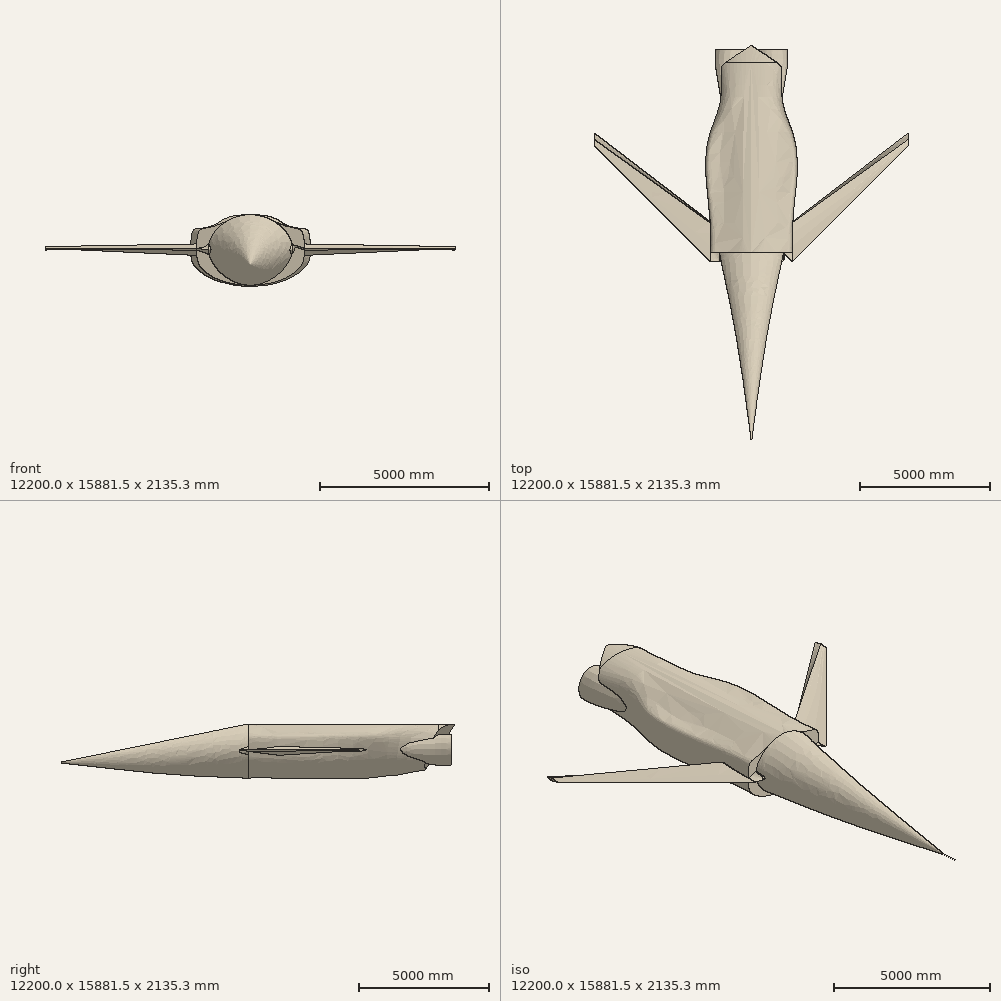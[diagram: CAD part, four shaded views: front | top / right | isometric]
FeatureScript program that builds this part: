
annotation { "Feature Type Name" : "Feature", "Feature Type Description" : "" }
export const myFeature = defineFeature(function(context is Context, id is Id, definition is map)
    precondition{}
    {
        {
            var Q0;
            Q0=qCreatedBy(makeId("Right.planeOp"),FACE);
            var sketch = newSketch(context, id + "F0", { "sketchPlane" : qUnion([Q0])});
            skLineSegment(sketch, "E0", {"start": v(0, 0) * mm, "end": v(-1750, 0) * mm});
            skLineSegment(sketch, "E1", {"start": v(-1750, 0) * mm, "end": v(-3500, 0) * mm});
            skLineSegment(sketch, "E2", {"start": v(-3500, 0) * mm, "end": v(-3500, -1000) * mm});
            skLineSegment(sketch, "E3", {"start": v(-3500, -1000) * mm, "end": v(-8500, -1000) * mm});
            skLineSegment(sketch, "E4", {"start": v(-8500, -1000) * mm, "end": v(-8500, -499.31) * mm});
            skLineSegment(sketch, "E5", {"start": v(-1151.4, 0) * mm, "end": v(-1151.4, 1000) * mm});
            skLineSegment(sketch, "E6", {"start": v(-1151.4, 1000) * mm, "end": v(-8500, -499.31) * mm});
            skLineSegment(sketch, "E7", {"start": v(-8500, -499.31) * mm, "end": v(-3500, -1000) * mm});
            skLineSegment(sketch, "E8", {"start": v(-3500, 0) * mm, "end": v(-3500, 520.82) * mm});
            skLineSegment(sketch, "E9", {"start": v(-8500, -499.31) * mm, "end": v(-8450, -499.31) * mm});
            skLineSegment(sketch, "E10", {"start": v(-8450, -499.31) * mm, "end": v(-8450, -489.1) * mm});
            skLineSegment(sketch, "E11", {"start": v(-8450, -499.31) * mm, "end": v(-8450, -504.32) * mm});
            skSolve(sketch);
        }
        {
            var Q0;
            Q0=sQuery(id+"F0.wireOp",EDGE,"E5");
            cPlane(context, id + "F1", {"entities" : qUnion([Q0]), "cplaneType" : CPlaneType.LINE_ANGLE, "offset" : 25 * mm, "angle" : 90 * degree, "oppositeDirection" : true, "width" : 150 * mm, "height" : 150 * mm});
        }
        {
            var Q0;
            Q0=qCreatedBy(id+"F1.planeOp",FACE);
            var sketch = newSketch(context, id + "F2", { "sketchPlane" : qUnion([Q0])});
            skPoint(sketch, "E12.middle", {"position": v(0, 0) * mm});
            skFitSpline(sketch, "E13", {"points": [v(0, 1000) * mm, v(-1060, 662.5) * mm, v(-1517.6, 506.84) * mm, v(-1600, 0) * mm, v(-1517.6, -506.84) * mm, v(-750, -1000) * mm, v(750, -1000) * mm, v(1517.6, -506.84) * mm, v(1600, 0) * mm, v(1517.6, 506.84) * mm, v(1060, 662.5) * mm, v(0, 1000) * mm]});
            skSolve(sketch);
        }
        {
            var Q0;
            Q0=qCreatedBy(makeId("Front.planeOp"),FACE);
            var sketch = newSketch(context, id + "F3", { "sketchPlane" : qUnion([Q0])});
            skPoint(sketch, "E14.middle", {"position": v(0, 0) * mm});
            skFitSpline(sketch, "E15", {"points": [v(0, 1000) * mm, v(-1060, 662.5) * mm, v(-1517.6, 506.84) * mm, v(-1600, 0) * mm, v(-1517.6, -506.84) * mm, v(-750, -1000) * mm, v(750, -1000) * mm, v(1517.6, -506.84) * mm, v(1600, 0) * mm, v(1517.6, 506.84) * mm, v(1060, 662.5) * mm, v(0, 1000) * mm]});
            skSolve(sketch);
        }
        {
            var Q0;
            Q0=qCreatedBy(makeId("Front.planeOp"),FACE);
            cPlane(context, id + "F4", {"entities" : qUnion([Q0]), "cplaneType" : CPlaneType.OFFSET, "offset" : 3500 * mm, "oppositeDirection" : true, "width" : 150 * mm, "height" : 150 * mm});
        }
        {
            var Q0;
            Q0=qCreatedBy(id+"F4.planeOp",FACE);
            var sketch = newSketch(context, id + "F5", { "sketchPlane" : qUnion([Q0])});
            skPoint(sketch, "E16.middle", {"position": v(0, 0) * mm});
            skFitSpline(sketch, "E17", {"points": [v(0, 1000) * mm, v(-1060, 662.5) * mm, v(-1517.6, 506.84) * mm, v(-1600, 0) * mm, v(-1517.6, -506.84) * mm, v(-750, -1000) * mm, v(750, -1000) * mm, v(1517.6, -506.84) * mm, v(1600, 0) * mm, v(1517.6, 506.84) * mm, v(1060, 662.5) * mm, v(0, 1000) * mm]});
            skSolve(sketch);
        }
        {
            var Q0;
            Q0=qCreatedBy(makeId("Front.planeOp"),FACE);
            cPlane(context, id + "F6", {"entities" : qUnion([Q0]), "cplaneType" : CPlaneType.OFFSET, "offset" : 4500 * mm, "oppositeDirection" : true, "width" : 150 * mm, "height" : 150 * mm});
        }
        {
            var Q0;
            Q0=qCreatedBy(id+"F6.planeOp",FACE);
            var sketch = newSketch(context, id + "F7", { "sketchPlane" : qUnion([Q0])});
            skPoint(sketch, "E18.middle", {"position": v(0, 0) * mm});
            skFitSpline(sketch, "E19", {"points": [v(0, 1000) * mm, v(-1060, 662.5) * mm, v(-1250, 0) * mm, v(-1060, -662.5) * mm, v(0, -1000) * mm, v(1060, -662.5) * mm, v(1250, 0) * mm, v(1060, 662.5) * mm, v(0, 1000) * mm]});
            skSolve(sketch);
        }
        {
            var Q0;
            Q0=qCreatedBy(makeId("Front.planeOp"),FACE);
            cPlane(context, id + "F8", {"entities" : qUnion([Q0]), "cplaneType" : CPlaneType.OFFSET, "offset" : 6232.05 * mm, "oppositeDirection" : true, "width" : 150 * mm, "height" : 150 * mm});
        }
        {
            var Q0;
            Q0=qCreatedBy(id+"F8.planeOp",FACE);
            var sketch = newSketch(context, id + "F9", { "sketchPlane" : qUnion([Q0])});
            skPoint(sketch, "E20.middle", {"position": v(0, 0) * mm});
            skFitSpline(sketch, "E21", {"points": [v(0, 1000) * mm, v(-1060, 662.5) * mm, v(-1250, 0) * mm, v(-848, -530) * mm, v(848, -530) * mm, v(1250, 0) * mm, v(1060, 662.5) * mm, v(0, 1000) * mm]});
            skSolve(sketch);
        }
        {
            var Q0;
            Q0=makeQuery(id+"F2.imprint","IMPRINT",FACE,{"disambiguationData":[TD([[makeQuery(id+"F2.imprint","IMPRINT",EDGE,{"derivedFrom":sQuery(id+"F2.wireOp",EDGE,"E13")}),1.0]])]});
            var Q1;
            Q1=makeQuery(id+"F3.imprint","IMPRINT",FACE,{"disambiguationData":[TD([[makeQuery(id+"F3.imprint","IMPRINT",EDGE,{"derivedFrom":sQuery(id+"F3.wireOp",EDGE,"E15")}),1.0]])]});
            var Q2;
            Q2=makeQuery(id+"F5.imprint","IMPRINT",FACE,{"disambiguationData":[TD([[makeQuery(id+"F5.imprint","IMPRINT",EDGE,{"derivedFrom":sQuery(id+"F5.wireOp",EDGE,"E17")}),1.0]])]});
            var Q3;
            Q3=makeQuery(id+"F7.imprint","IMPRINT",FACE,{"disambiguationData":[TD([[makeQuery(id+"F7.imprint","IMPRINT",EDGE,{"derivedFrom":sQuery(id+"F7.wireOp",EDGE,"E19")}),1.0]])]});
            var Q4;
            Q4=makeQuery(id+"F9.imprint","IMPRINT",FACE,{"disambiguationData":[TD([[makeQuery(id+"F9.imprint","IMPRINT",EDGE,{"derivedFrom":sQuery(id+"F9.wireOp",EDGE,"E21")}),1.0]])]});
            loft(context, id + "F10", {"sheetProfilesArray" : [{ "sheetProfileEntities" : qUnion([Q0]) }, { "sheetProfileEntities" : qUnion([Q1]) }, { "sheetProfileEntities" : qUnion([Q2]) }, { "sheetProfileEntities" : qUnion([Q3]) }, { "sheetProfileEntities" : qUnion([Q4]) }]});
        }
        {
            var Q0;
            Q0=makeQuery(id+"F10.opLoft","CAP_FACE",FACE,{"disambiguationData":[OSD([makeQuery(id+"F9.imprint","IMPRINT",FACE,{"disambiguationData":[TD([[makeQuery(id+"F9.imprint","IMPRINT",EDGE,{"derivedFrom":sQuery(id+"F9.wireOp",EDGE,"E21")}),1.0]])]})])],"isStart":true});
            extrude(context, id + "F11", {"entities" : qUnion([Q0]), "operationType" : NewBodyOperationType.ADD, "depth" : 649.4 * mm, "offsetDistance" : 25 * mm});
        }
        {
            var Q0;
            Q0=qCreatedBy(makeId("Right.planeOp"),FACE);
            var sketch = newSketch(context, id + "F12", { "sketchPlane" : qUnion([Q0])});
            skLineSegment(sketch, "E22", {"start": v(0, 0) * mm, "end": v(4500, 0) * mm});
            skLineSegment(sketch, "E23", {"start": v(4500, 0) * mm, "end": v(6232.05, 0) * mm});
            skLineSegment(sketch, "E24", {"start": v(4500, 0) * mm, "end": v(4500, 1000) * mm});
            skLineSegment(sketch, "E25", {"start": v(4500, 1000) * mm, "end": v(6881.46, 1000) * mm});
            skLineSegment(sketch, "E26", {"start": v(6881.46, 1000) * mm, "end": v(6881.46, -1000) * mm});
            skLineSegment(sketch, "E27", {"start": v(6881.46, 1000) * mm, "end": v(6232.05, 0) * mm});
            skLineSegment(sketch, "E28", {"start": v(6232.05, 0) * mm, "end": v(5582.64, -1000) * mm});
            skLineSegment(sketch, "E29", {"start": v(5582.64, -1000) * mm, "end": v(6881.46, -1000) * mm});
            skSolve(sketch);
        }
        {
            var Q0;
            Q0=makeQuery(id+"F12.imprint","IMPRINT",FACE,{"disambiguationData":[TD([[makeQuery(id+"F12.imprint","IMPRINT",EDGE,{"derivedFrom":sQuery(id+"F12.wireOp",EDGE,"E26")}),-1.0]])]});
            var Q1;
            Q1=sQuery(id+"F12.wireOp",EDGE,"E25");
            revolve(context, id + "F13", {"operationType" : NewBodyOperationType.REMOVE, "entities" : qUnion([Q0]), "axis" : qUnion([Q1]), "revolveType" : RevolveType.SYMMETRIC, "oppositeDirection" : true, "angle" : 182 * degree});
        }
        {
            var Q0;
            Q0=qCreatedBy(id+"F1.planeOp",FACE);
            var sketch = newSketch(context, id + "F14", { "sketchPlane" : qUnion([Q0])});
            skFitSpline(sketch, "E30", {"points": [v(0, 1000) * mm, v(-1250, 0) * mm, v(0, -1099.92) * mm, v(1250, 0) * mm, v(0, 1000) * mm]});
            skSolve(sketch);
        }
        {
            var Q0;
            Q0=qCreatedBy(makeId("Front.planeOp"),FACE);
            cPlane(context, id + "F15", {"entities" : qUnion([Q0]), "cplaneType" : CPlaneType.OFFSET, "offset" : 3500 * mm, "width" : 150 * mm, "height" : 150 * mm});
        }
        {
            var Q0;
            Q0=qCreatedBy(id+"F15.planeOp",FACE);
            var sketch = newSketch(context, id + "F16", { "sketchPlane" : qUnion([Q0])});
            skCircle(sketch, "E31", {"center": v(0, -239.59) * mm, "radius": 760.41 * mm});
            skSolve(sketch);
        }
        {
            var Q0;
            Q0=qCreatedBy(makeId("Front.planeOp"),FACE);
            cPlane(context, id + "F17", {"entities" : qUnion([Q0]), "cplaneType" : CPlaneType.OFFSET, "offset" : 8450 * mm, "width" : 150 * mm, "height" : 150 * mm});
        }
        {
            var Q0;
            Q0=qCreatedBy(id+"F17.planeOp",FACE);
            var sketch = newSketch(context, id + "F18", { "sketchPlane" : qUnion([Q0])});
            skCircle(sketch, "E32", {"center": v(0, -496.71) * mm, "radius": 7.6 * mm});
            skSolve(sketch);
        }
        {
            var Q1;
            Q1=makeQuery(id+"F18.imprint","IMPRINT",FACE,{"disambiguationData":[TD([[makeQuery(id+"F18.imprint","IMPRINT",EDGE,{"derivedFrom":sQuery(id+"F18.wireOp",EDGE,"E32")}),1.0]])]});
            var Q2;
            Q2=makeQuery(id+"F16.imprint","IMPRINT",FACE,{"disambiguationData":[TD([[makeQuery(id+"F16.imprint","IMPRINT",EDGE,{"derivedFrom":sQuery(id+"F16.wireOp",EDGE,"E31")}),1.0]])]});
            var Q3;
            Q3=makeQuery(id+"F14.imprint","IMPRINT",FACE,{"disambiguationData":[TD([[makeQuery(id+"F14.imprint","IMPRINT",EDGE,{"derivedFrom":sQuery(id+"F14.wireOp",EDGE,"E30")}),1.0]])]});
            loft(context, id + "F19", {"operationType" : NewBodyOperationType.ADD, "sheetProfilesArray" : [{ "sheetProfileEntities" : qUnion([Q1]) }, { "sheetProfileEntities" : qUnion([Q2]) }, { "sheetProfileEntities" : qUnion([Q3]) }]});
        }
        {
            var Q0;
            Q0=makeQuery(id+"F19.opLoft","CAP_FACE",FACE,{"disambiguationData":[OSD([makeQuery(id+"F18.imprint","IMPRINT",FACE,{"disambiguationData":[TD([[makeQuery(id+"F18.imprint","IMPRINT",EDGE,{"derivedFrom":sQuery(id+"F18.wireOp",EDGE,"E32")}),1.0]])]})])],"isStart":true});
            extrude(context, id + "F20", {"entities" : qUnion([Q0]), "operationType" : NewBodyOperationType.ADD, "depth" : 550 * mm, "offsetDistance" : 25 * mm});
        }
        {
            var Q0;
            Q0=qCreatedBy(makeId("Front.planeOp"),FACE);
            cPlane(context, id + "F21", {"entities" : qUnion([Q0]), "cplaneType" : CPlaneType.OFFSET, "offset" : 3500 * mm, "oppositeDirection" : true, "width" : 150 * mm, "height" : 150 * mm});
        }
        {
            var Q0;
            Q0=qCreatedBy(id+"F21.planeOp",FACE);
            var sketch = newSketch(context, id + "F22", { "sketchPlane" : qUnion([Q0])});
            skCircle(sketch, "E33", {"center": v(-800, 0) * mm, "radius": 600 * mm});
            skCircle(sketch, "E34", {"center": v(800, 0) * mm, "radius": 600 * mm});
            skSolve(sketch);
        }
        {
            var Q0;
            Q0=qCreatedBy(makeId("Front.planeOp"),FACE);
            cPlane(context, id + "F23", {"entities" : qUnion([Q0]), "cplaneType" : CPlaneType.OFFSET, "offset" : 4500 * mm, "oppositeDirection" : true, "width" : 150 * mm, "height" : 150 * mm});
        }
        {
            var Q0;
            Q0=qCreatedBy(id+"F23.planeOp",FACE);
            var sketch = newSketch(context, id + "F24", { "sketchPlane" : qUnion([Q0])});
            skCircle(sketch, "E35", {"center": v(-800, 0) * mm, "radius": 400 * mm});
            skCircle(sketch, "E36", {"center": v(800, 0) * mm, "radius": 400 * mm});
            skSolve(sketch);
        }
        {
            var Q0;
            Q0=qCreatedBy(makeId("Front.planeOp"),FACE);
            cPlane(context, id + "F25", {"entities" : qUnion([Q0]), "cplaneType" : CPlaneType.OFFSET, "offset" : 6232.05 * mm, "oppositeDirection" : true, "width" : 150 * mm, "height" : 150 * mm});
        }
        {
            var Q0;
            Q0=qCreatedBy(id+"F25.planeOp",FACE);
            var sketch = newSketch(context, id + "F26", { "sketchPlane" : qUnion([Q0])});
            skCircle(sketch, "E37", {"center": v(-800, 0) * mm, "radius": 600 * mm});
            skCircle(sketch, "E38", {"center": v(800, 0) * mm, "radius": 600 * mm});
            skSolve(sketch);
        }
        {
            var Q0;
            Q0=qCreatedBy(makeId("Front.planeOp"),FACE);
            cPlane(context, id + "F27", {"entities" : qUnion([Q0]), "cplaneType" : CPlaneType.OFFSET, "offset" : 6732.05 * mm, "oppositeDirection" : true, "width" : 150 * mm, "height" : 150 * mm});
        }
        {
            var Q0;
            Q0=qCreatedBy(id+"F27.planeOp",FACE);
            var sketch = newSketch(context, id + "F28", { "sketchPlane" : qUnion([Q0])});
            skCircle(sketch, "E39", {"center": v(-800, 0) * mm, "radius": 600 * mm});
            skCircle(sketch, "E40", {"center": v(800, 0) * mm, "radius": 600 * mm});
            skSolve(sketch);
        }
        {
            var Q0;
            Q0=makeQuery(id+"F22.imprint","IMPRINT",FACE,{"disambiguationData":[TD([[makeQuery(id+"F22.imprint","IMPRINT",EDGE,{"derivedFrom":sQuery(id+"F22.wireOp",EDGE,"E33")}),1.0]])]});
            var Q1;
            Q1=makeQuery(id+"F24.imprint","IMPRINT",FACE,{"disambiguationData":[TD([[makeQuery(id+"F24.imprint","IMPRINT",EDGE,{"derivedFrom":sQuery(id+"F24.wireOp",EDGE,"E35")}),1.0]])]});
            var Q2;
            Q2=makeQuery(id+"F26.imprint","IMPRINT",FACE,{"disambiguationData":[TD([[makeQuery(id+"F26.imprint","IMPRINT",EDGE,{"derivedFrom":sQuery(id+"F26.wireOp",EDGE,"E37")}),1.0]])]});
            var Q3;
            Q3=makeQuery(id+"F28.imprint","IMPRINT",FACE,{"disambiguationData":[TD([[makeQuery(id+"F28.imprint","IMPRINT",EDGE,{"derivedFrom":sQuery(id+"F28.wireOp",EDGE,"E39")}),1.0]])]});
            loft(context, id + "F29", {"sheetProfilesArray" : [{ "sheetProfileEntities" : qUnion([Q0]) }, { "sheetProfileEntities" : qUnion([Q1]) }, { "sheetProfileEntities" : qUnion([Q2]) }, { "sheetProfileEntities" : qUnion([Q3]) }]});
        }
        {
            var Q0;
            Q0=makeQuery(id+"F22.imprint","IMPRINT",FACE,{"disambiguationData":[TD([[makeQuery(id+"F22.imprint","IMPRINT",EDGE,{"derivedFrom":sQuery(id+"F22.wireOp",EDGE,"E34")}),1.0]])]});
            var Q1;
            Q1=makeQuery(id+"F24.imprint","IMPRINT",FACE,{"disambiguationData":[TD([[makeQuery(id+"F24.imprint","IMPRINT",EDGE,{"derivedFrom":sQuery(id+"F24.wireOp",EDGE,"E36")}),1.0]])]});
            var Q2;
            Q2=makeQuery(id+"F26.imprint","IMPRINT",FACE,{"disambiguationData":[TD([[makeQuery(id+"F26.imprint","IMPRINT",EDGE,{"derivedFrom":sQuery(id+"F26.wireOp",EDGE,"E38")}),1.0]])]});
            var Q3;
            Q3=makeQuery(id+"F28.imprint","IMPRINT",FACE,{"disambiguationData":[TD([[makeQuery(id+"F28.imprint","IMPRINT",EDGE,{"derivedFrom":sQuery(id+"F28.wireOp",EDGE,"E40")}),1.0]])]});
            loft(context, id + "F30", {"sheetProfilesArray" : [{ "sheetProfileEntities" : qUnion([Q0]) }, { "sheetProfileEntities" : qUnion([Q1]) }, { "sheetProfileEntities" : qUnion([Q2]) }, { "sheetProfileEntities" : qUnion([Q3]) }]});
        }
        {
            var Q0;
            Q0=qCreatedBy(makeId("Right.planeOp"),FACE);
            var sketch = newSketch(context, id + "F31", { "sketchPlane" : qUnion([Q0])});
            skFitSpline(sketch, "E41", {"points": [v(-1500, -50) * mm, v(0, 250) * mm, v(3000, 0) * mm, v(0, -250) * mm, v(-1500, -50) * mm]});
            skSolve(sketch);
        }
        {
            var Q0;
            Q0=qCreatedBy(makeId("Right.planeOp"),FACE);
            cPlane(context, id + "F32", {"entities" : qUnion([Q0]), "cplaneType" : CPlaneType.OFFSET, "offset" : 1600 * mm, "oppositeDirection" : true, "width" : 150 * mm, "height" : 150 * mm});
        }
        {
            var Q0;
            Q0=qCreatedBy(id+"F32.planeOp",FACE);
            var sketch = newSketch(context, id + "F33", { "sketchPlane" : qUnion([Q0])});
            skFitSpline(sketch, "E42", {"points": [v(-1500, 0) * mm, v(1000, 250) * mm, v(3500, 0) * mm], "startDerivative": vector(7500, 0) * mm, "endDerivative": vector(7500, 0) * mm});
            skFitSpline(sketch, "E43", {"points": [v(-1500, 0) * mm, v(1000, -250) * mm, v(3500, 0) * mm], "startDerivative": vector(5000, -750) * mm, "endDerivative": vector(7500, 0) * mm});
            skSolve(sketch);
        }
        {
            var Q0;
            Q0=qCreatedBy(makeId("Right.planeOp"),FACE);
            cPlane(context, id + "F34", {"entities" : qUnion([Q0]), "cplaneType" : CPlaneType.OFFSET, "offset" : 1600 * mm, "width" : 150 * mm, "height" : 150 * mm});
        }
        {
            var Q0;
            Q0=qCreatedBy(id+"F34.planeOp",FACE);
            var sketch = newSketch(context, id + "F35", { "sketchPlane" : qUnion([Q0])});
            skFitSpline(sketch, "E44", {"points": [v(-1500, 0) * mm, v(1000, 250) * mm, v(3500, 0) * mm], "startDerivative": vector(7500, 0) * mm, "endDerivative": vector(7500, 0) * mm});
            skFitSpline(sketch, "E45", {"points": [v(-1500, 0) * mm, v(1000, -250) * mm, v(3500, 0) * mm], "startDerivative": vector(5000, -750) * mm, "endDerivative": vector(7500, 0) * mm});
            skSolve(sketch);
        }
        {
            var Q0;
            Q0=qCreatedBy(makeId("Right.planeOp"),FACE);
            cPlane(context, id + "F36", {"entities" : qUnion([Q0]), "cplaneType" : CPlaneType.OFFSET, "offset" : 6100 * mm, "oppositeDirection" : true, "width" : 150 * mm, "height" : 150 * mm});
        }
        {
            var Q0;
            Q0=qCreatedBy(id+"F36.planeOp",FACE);
            var sketch = newSketch(context, id + "F37", { "sketchPlane" : qUnion([Q0])});
            skFitSpline(sketch, "E46", {"points": [v(3000, 0) * mm, v(3250, 50) * mm, v(3500, 0) * mm], "startDerivative": vector(750, 0) * mm, "endDerivative": vector(750, 0) * mm});
            skFitSpline(sketch, "E47", {"points": [v(3000, 0) * mm, v(3250, -50) * mm, v(3500, 0) * mm], "startDerivative": vector(500, -150) * mm, "endDerivative": vector(750, 0) * mm});
            skSolve(sketch);
        }
        {
            var Q0;
            Q0=qCreatedBy(makeId("Right.planeOp"),FACE);
            cPlane(context, id + "F38", {"entities" : qUnion([Q0]), "cplaneType" : CPlaneType.OFFSET, "offset" : 6100 * mm, "width" : 150 * mm, "height" : 150 * mm});
        }
        {
            var Q0;
            Q0=qCreatedBy(id+"F38.planeOp",FACE);
            var sketch = newSketch(context, id + "F39", { "sketchPlane" : qUnion([Q0])});
            skFitSpline(sketch, "E48", {"points": [v(3000, 0) * mm, v(3250, 50) * mm, v(3500, 0) * mm], "startDerivative": vector(750, 0) * mm, "endDerivative": vector(750, 0) * mm});
            skFitSpline(sketch, "E49", {"points": [v(3000, 0) * mm, v(3250, -50) * mm, v(3500, 0) * mm], "startDerivative": vector(500, -150) * mm, "endDerivative": vector(750, 0) * mm});
            skSolve(sketch);
        }
        {
            var Q0;
            Q0 = qSketchRegion(id + "F31", true);
            extrude(context, id + "F40", {"entities" : qUnion([Q0]), "endBound" : BoundingType.SYMMETRIC, "depth" : 2500 * mm, "offsetDistance" : 25 * mm});
        }
        {
            var Q1;
            Q1=makeQuery(id+"F40.opExtrude","CAP_FACE",FACE,{"disambiguationData":[OSD([sQuery(id+"F31.wireOp",EDGE,"E41")])],"isStart":true});
            var Q2;
            {var subQ0=sQuery(id+"F33.wireOp",EDGE,"E42");Q2=makeQuery(id+"F33.imprint","IMPRINT",FACE,{"disambiguationData":[TD([[makeQuery(id+"F33.imprint","IMPRINT",EDGE,{"derivedFrom":subQ0}),-1.0]])]});}
            loft(context, id + "F41", {"operationType" : NewBodyOperationType.ADD, "sheetProfilesArray" : [{ "sheetProfileEntities" : qUnion([Q1]) }, { "sheetProfileEntities" : qUnion([Q2]) }]});
        }
        {
            var Q1;
            Q1=makeQuery(id+"F40.opExtrude","CAP_FACE",FACE,{"disambiguationData":[OSD([sQuery(id+"F31.wireOp",EDGE,"E41")])],"isStart":false});
            var Q2;
            {var subQ0=sQuery(id+"F35.wireOp",EDGE,"E44");Q2=makeQuery(id+"F35.imprint","IMPRINT",FACE,{"disambiguationData":[TD([[makeQuery(id+"F35.imprint","IMPRINT",EDGE,{"derivedFrom":subQ0}),-1.0]])]});}
            loft(context, id + "F42", {"operationType" : NewBodyOperationType.ADD, "sheetProfilesArray" : [{ "sheetProfileEntities" : qUnion([Q1]) }, { "sheetProfileEntities" : qUnion([Q2]) }]});
        }
        {
            var Q1;
            {var subQ0=sQuery(id+"F33.wireOp",EDGE,"E42");Q1=makeQuery(id+"F41.opLoft","CAP_FACE",FACE,{"disambiguationData":[OSD([makeQuery(id+"F33.imprint","IMPRINT",FACE,{"disambiguationData":[TD([[makeQuery(id+"F33.imprint","IMPRINT",EDGE,{"derivedFrom":subQ0}),-1.0]])]})])],"isStart":true});}
            var Q2;
            {var subQ0=sQuery(id+"F37.wireOp",EDGE,"E46");Q2=makeQuery(id+"F37.imprint","IMPRINT",FACE,{"disambiguationData":[TD([[makeQuery(id+"F37.imprint","IMPRINT",EDGE,{"derivedFrom":subQ0}),-1.0]])]});}
            loft(context, id + "F43", {"operationType" : NewBodyOperationType.ADD, "sheetProfilesArray" : [{ "sheetProfileEntities" : qUnion([Q1]) }, { "sheetProfileEntities" : qUnion([Q2]) }]});
        }
        {
            var Q1;
            {var subQ0=sQuery(id+"F35.wireOp",EDGE,"E44");Q1=makeQuery(id+"F42.opLoft","CAP_FACE",FACE,{"disambiguationData":[OSD([makeQuery(id+"F35.imprint","IMPRINT",FACE,{"disambiguationData":[TD([[makeQuery(id+"F35.imprint","IMPRINT",EDGE,{"derivedFrom":subQ0}),-1.0]])]})])],"isStart":true});}
            var Q2;
            {var subQ0=sQuery(id+"F39.wireOp",EDGE,"E48");Q2=makeQuery(id+"F39.imprint","IMPRINT",FACE,{"disambiguationData":[TD([[makeQuery(id+"F39.imprint","IMPRINT",EDGE,{"derivedFrom":subQ0}),-1.0]])]});}
            loft(context, id + "F44", {"operationType" : NewBodyOperationType.ADD, "sheetProfilesArray" : [{ "sheetProfileEntities" : qUnion([Q1]) }, { "sheetProfileEntities" : qUnion([Q2]) }]});
        }
    });
